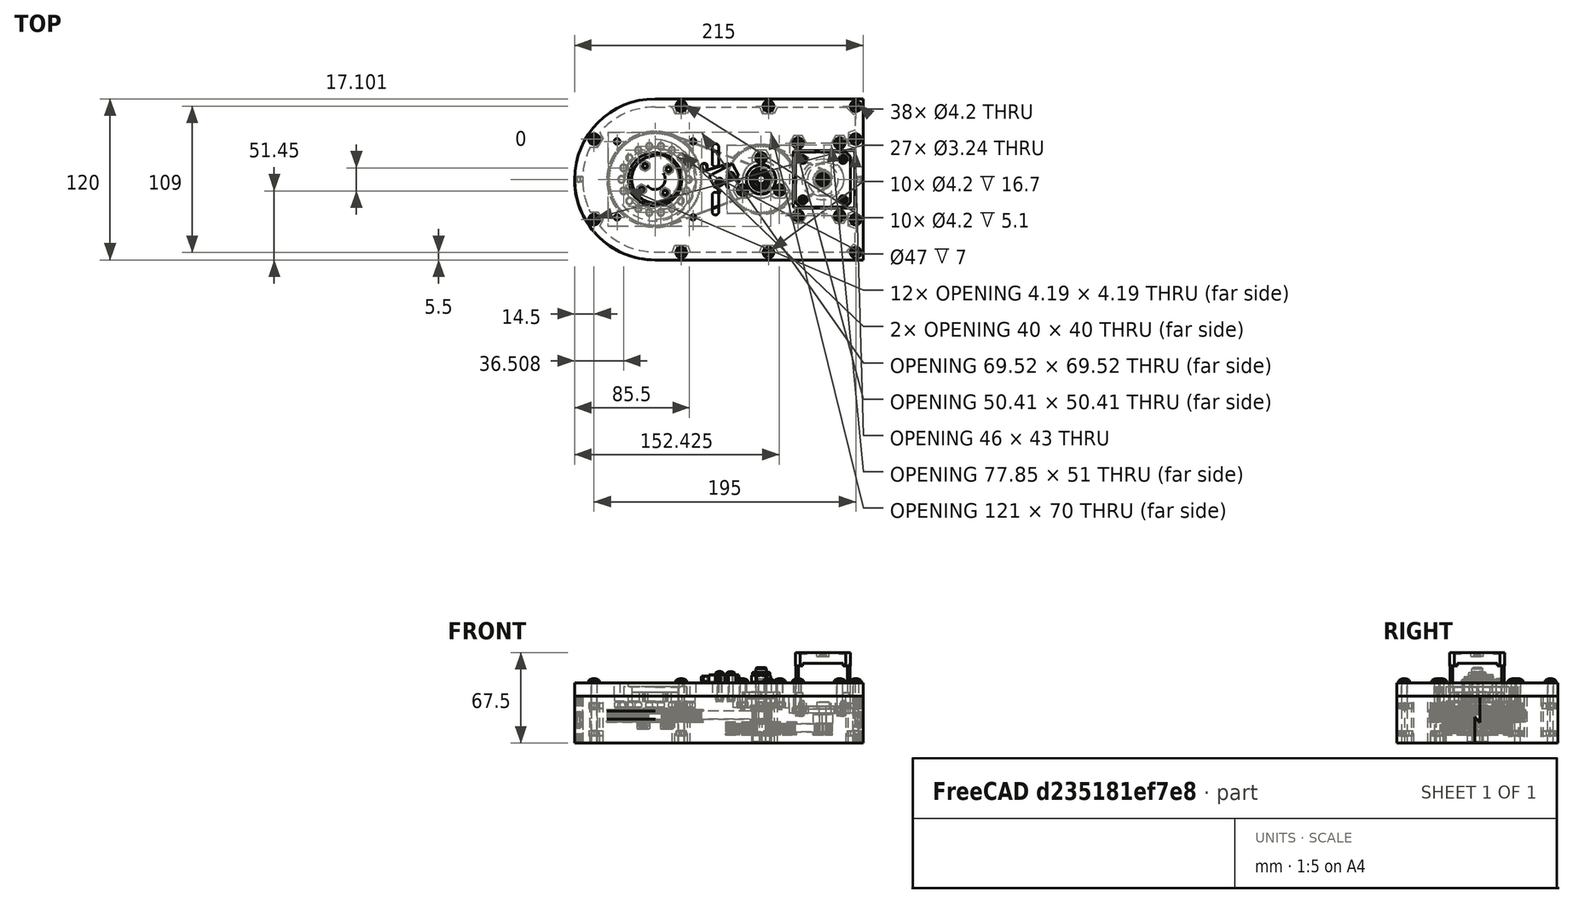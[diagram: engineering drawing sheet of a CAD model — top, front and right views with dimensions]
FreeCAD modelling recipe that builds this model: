
FCSTD DOCUMENT  (FreeCAD 0.19R24276 (Git))
Label: Base_a2p
License: All rights reserved
LicenseURL: http://en.wikipedia.org/wiki/All_rights_reserved
objects: Part::FeaturePython×75, App::FeaturePython×48, Spreadsheet::Sheet×2
note: 75 computed .brp shape members not serialized (recipe doc carries the construction recipe); baked Part::Feature solids carry a one-line shape summary decoded from their .brp

FEATURE [Part::FeaturePython] b_Base_half_wall_001_  label="Base_half-wall_001"  # a2plus imported part (geometry in sourceFile) (typed FeaturePython)
  a2p_Version = V0.1
  fixedPosition = true
  objectType = a2pPart
  sourceFile = ./Base_half-wall.FCStd
  subassemblyImport = false
  timeLastImport = 1.62051e+09
  updateColors = true
FEATURE [Part::FeaturePython] b_Base_half_wall_001_001  label="Base_half-wall_002"  # a2plus imported part (geometry in sourceFile) (typed FeaturePython)
  Placement = pos=(1e-15,-2.9e-14,-1.35227e-08) rot=(1,0,0;3.14159rad)
  a2p_Version = V0.1
  fixedPosition = false
  objectType = a2pPart
  sourceFile = ./Base_half-wall.FCStd
  subassemblyImport = false
  timeLastImport = 1.62051e+09
  updateColors = true
FEATURE [App::FeaturePython] circularEdge_001  label="circularEdge_001__Base_half-wall_002"  # a2plus constraint (typed FeaturePython)
  Object1 = b_Base_half_wall_001_
  Object2 = b_Base_half_wall_001_001
  ParentTreeObject = -> b_Base_half_wall_001_
  SubElement1 = Edge96
  SubElement2 = Edge52
  Suppressed = false
  Type = circularEdge
  directionConstraint = 1
  lockRotation = true
  offset = 0
FEATURE [App::FeaturePython] circularEdge_001_mirror  label="circularEdge_001__Base_half-wall_001"  # a2plus constraint (typed FeaturePython)
  Object1 = b_Base_half_wall_001_
  Object2 = b_Base_half_wall_001_001
  ParentTreeObject = -> b_Base_half_wall_001_001
  SubElement1 = Edge96
  SubElement2 = Edge52
  Suppressed = false
  Type = circularEdge
  directionConstraint = 1
  lockRotation = true
  offset = 0
FEATURE [Part::FeaturePython] b_Base_plate_001_  label="Base_plate_001"  # a2plus imported part (geometry in sourceFile) (typed FeaturePython)
  Placement = pos=(5.66811e-10,1.89089e-08,27.5) rot=(1,0,0;3.14159rad)
  a2p_Version = V0.1
  fixedPosition = false
  objectType = a2pPart
  sourceFile = ./Base_plate.FCStd
  subassemblyImport = false
  timeLastImport = 1.62051e+09
  updateColors = true
FEATURE [App::FeaturePython] circularEdge_002  label="circularEdge_002__Base_half-wall_001"  # a2plus constraint (typed FeaturePython)
  Object1 = b_Base_plate_001_
  Object2 = b_Base_half_wall_001_
  ParentTreeObject = -> b_Base_plate_001_
  SubElement1 = Edge4
  SubElement2 = Edge100
  Suppressed = false
  Type = circularEdge
  directionConstraint = 1
  lockRotation = true
  offset = 0
FEATURE [App::FeaturePython] circularEdge_002_mirror  label="circularEdge_002__Base_plate_001"  # a2plus constraint (typed FeaturePython)
  Object1 = b_Base_plate_001_
  Object2 = b_Base_half_wall_001_
  ParentTreeObject = -> b_Base_half_wall_001_
  SubElement1 = Edge4
  SubElement2 = Edge100
  Suppressed = false
  Type = circularEdge
  directionConstraint = 1
  lockRotation = true
  offset = 0
FEATURE [Part::FeaturePython] b_Stepper_NEMA_17____20mm_shaft1_001_  label="Stepper NEMA 17 -  20mm shaft1_001"  # a2plus imported part (geometry in sourceFile) (typed FeaturePython)
  Placement = pos=(162.191,8.47956,71.0261) rot=(-0.708681,0.705529,0;3.14159rad)
  a2p_Version = V0.1
  fixedPosition = false
  objectType = a2pPart
  sourceFile = ./Stepper NEMA 17 -  20mm shaft.step
  subassemblyImport = false
  timeLastImport = 1.62049e+09
  updateColors = true
FEATURE [Part::FeaturePython] b_Base_motor_bracket_001_  label="Base_motor_bracket_001"  # a2plus imported part (geometry in sourceFile) (typed FeaturePython)
  Placement = pos=(122,-3.40918e-07,5) rot=(0,0,1;1.5708rad)
  a2p_Version = V0.1
  fixedPosition = false
  objectType = a2pPart
  sourceFile = ./Base_motor_bracket.FCStd
  subassemblyImport = false
  timeLastImport = 1.62051e+09
  updateColors = true
FEATURE [App::FeaturePython] circularEdge_003  label="circularEdge_003__Base_plate_001"  # a2plus constraint (typed FeaturePython)
  Object1 = b_Base_motor_bracket_001_
  Object2 = b_Base_plate_001_
  ParentTreeObject = -> b_Base_motor_bracket_001_
  SubElement1 = Edge30
  SubElement2 = Edge77
  Suppressed = false
  Type = circularEdge
  directionConstraint = 1
  lockRotation = false
  offset = 0
FEATURE [App::FeaturePython] circularEdge_003_mirror  label="circularEdge_003__Base_motor_bracket_001"  # a2plus constraint (typed FeaturePython)
  Object1 = b_Base_motor_bracket_001_
  Object2 = b_Base_plate_001_
  ParentTreeObject = -> b_Base_plate_001_
  SubElement1 = Edge30
  SubElement2 = Edge77
  Suppressed = false
  Type = circularEdge
  directionConstraint = 1
  lockRotation = false
  offset = 0
FEATURE [App::FeaturePython] axisCoincident_001  label="axisCoincident_001__Base_plate_001"  # a2plus constraint (typed FeaturePython)
  Object1 = b_Base_motor_bracket_001_
  Object2 = b_Base_plate_001_
  ParentTreeObject = -> b_Base_motor_bracket_001_
  SubElement1 = Face29
  SubElement2 = Face40
  Suppressed = false
  Type = axial
  directionConstraint = 1
  lockRotation = false
FEATURE [App::FeaturePython] axisCoincident_001_mirror  label="axisCoincident_001__Base_motor_bracket_001"  # a2plus constraint (typed FeaturePython)
  Object1 = b_Base_motor_bracket_001_
  Object2 = b_Base_plate_001_
  ParentTreeObject = -> b_Base_plate_001_
  SubElement1 = Face29
  SubElement2 = Face40
  Suppressed = false
  Type = axial
  directionConstraint = 1
  lockRotation = false
FEATURE [App::FeaturePython] planeCoincident_001  label="planeCoincident_001__Base_motor_bracket_001"  # a2plus constraint (typed FeaturePython)
  Object1 = b_Stepper_NEMA_17____20mm_shaft1_001_
  Object2 = b_Base_motor_bracket_001_
  ParentTreeObject = -> b_Stepper_NEMA_17____20mm_shaft1_001_
  SubElement1 = Face140
  SubElement2 = Face31
  Suppressed = false
  Type = plane
  directionConstraint = 1
  offset = 0
FEATURE [App::FeaturePython] planeCoincident_001_mirror  label="planeCoincident_001__Stepper NEMA 17 -  20mm shaft1_001"  # a2plus constraint (typed FeaturePython)
  Object1 = b_Stepper_NEMA_17____20mm_shaft1_001_
  Object2 = b_Base_motor_bracket_001_
  ParentTreeObject = -> b_Base_motor_bracket_001_
  SubElement1 = Face140
  SubElement2 = Face31
  Suppressed = false
  Type = plane
  directionConstraint = 1
  offset = 0
FEATURE [Part::FeaturePython] b_Base_dual_bearing_608_holder_001_  label="Base_dual_bearing_608_holder_001"  # a2plus imported part (geometry in sourceFile) (typed FeaturePython)
  Placement = pos=(79,3.47e-08,9) rot=(0,0,-1;1.5708rad)
  a2p_Version = V0.1
  fixedPosition = false
  objectType = a2pPart
  sourceFile = ./Base_dual_bearing_608_holder.FCStd
  subassemblyImport = false
  timeLastImport = 1.62052e+09
  updateColors = true
FEATURE [Part::FeaturePython] b_Ball_bearing_6081_001_  label="Ball_bearing_6081_001"  # a2plus imported part (geometry in sourceFile) (typed FeaturePython)
  Placement = pos=(79,4.49238e-08,9) rot=(0.999356,0.025383,0.025383;1.57144rad)
  a2p_Version = V0.1
  fixedPosition = false
  objectType = a2pPart
  sourceFile = ./Ball_bearing_608.step
  subassemblyImport = false
  timeLastImport = 1.62049e+09
  updateColors = true
FEATURE [App::FeaturePython] circularEdge_004  label="circularEdge_004__Base_plate_001"  # a2plus constraint (typed FeaturePython)
  Object1 = b_Base_dual_bearing_608_holder_001_
  Object2 = b_Base_plate_001_
  ParentTreeObject = -> b_Base_dual_bearing_608_holder_001_
  SubElement1 = Edge15
  SubElement2 = Edge158
  Suppressed = false
  Type = circularEdge
  directionConstraint = 1
  lockRotation = false
  offset = 0
FEATURE [App::FeaturePython] circularEdge_004_mirror  label="circularEdge_004__Base_dual_bearing_608_holder_001"  # a2plus constraint (typed FeaturePython)
  Object1 = b_Base_dual_bearing_608_holder_001_
  Object2 = b_Base_plate_001_
  ParentTreeObject = -> b_Base_plate_001_
  SubElement1 = Edge15
  SubElement2 = Edge158
  Suppressed = false
  Type = circularEdge
  directionConstraint = 1
  lockRotation = false
  offset = 0
FEATURE [App::FeaturePython] axisCoincident_004  label="axisCoincident_004__Base_plate_001"  # a2plus constraint (typed FeaturePython)
  Object1 = b_Base_dual_bearing_608_holder_001_
  Object2 = b_Base_plate_001_
  ParentTreeObject = -> b_Base_dual_bearing_608_holder_001_
  SubElement1 = Face33
  SubElement2 = Face44
  Suppressed = false
  Type = axial
  directionConstraint = 1
  lockRotation = false
FEATURE [App::FeaturePython] axisCoincident_004_mirror  label="axisCoincident_004__Base_dual_bearing_608_holder_001"  # a2plus constraint (typed FeaturePython)
  Object1 = b_Base_dual_bearing_608_holder_001_
  Object2 = b_Base_plate_001_
  ParentTreeObject = -> b_Base_plate_001_
  SubElement1 = Face33
  SubElement2 = Face44
  Suppressed = false
  Type = axial
  directionConstraint = 1
  lockRotation = false
FEATURE [App::FeaturePython] axisCoincident_005  label="axisCoincident_005__Base_dual_bearing_608_holder_001"  # a2plus constraint (typed FeaturePython)
  Object1 = b_Ball_bearing_6081_001_
  Object2 = b_Base_dual_bearing_608_holder_001_
  ParentTreeObject = -> b_Ball_bearing_6081_001_
  SubElement1 = Face15
  SubElement2 = Face25
  Suppressed = false
  Type = axial
  directionConstraint = 0
  lockRotation = false
FEATURE [App::FeaturePython] axisCoincident_005_mirror  label="axisCoincident_005__Ball_bearing_6081_001"  # a2plus constraint (typed FeaturePython)
  Object1 = b_Ball_bearing_6081_001_
  Object2 = b_Base_dual_bearing_608_holder_001_
  ParentTreeObject = -> b_Base_dual_bearing_608_holder_001_
  SubElement1 = Face15
  SubElement2 = Face25
  Suppressed = false
  Type = axial
  directionConstraint = 0
  lockRotation = false
FEATURE [App::FeaturePython] planeCoincident_002  label="planeCoincident_002__Base_dual_bearing_608_holder_001"  # a2plus constraint (typed FeaturePython)
  Object1 = b_Ball_bearing_6081_001_
  Object2 = b_Base_dual_bearing_608_holder_001_
  ParentTreeObject = -> b_Ball_bearing_6081_001_
  SubElement1 = Face13
  SubElement2 = Face51
  Suppressed = false
  Type = plane
  directionConstraint = 1
  offset = 0
FEATURE [App::FeaturePython] planeCoincident_002_mirror  label="planeCoincident_002__Ball_bearing_6081_001"  # a2plus constraint (typed FeaturePython)
  Object1 = b_Ball_bearing_6081_001_
  Object2 = b_Base_dual_bearing_608_holder_001_
  ParentTreeObject = -> b_Base_dual_bearing_608_holder_001_
  SubElement1 = Face13
  SubElement2 = Face51
  Suppressed = false
  Type = plane
  directionConstraint = 1
  offset = 0
FEATURE [Part::FeaturePython] b_Ball_bearing_6081_001_001  label="Ball_bearing_6081_002"  # a2plus imported part (geometry in sourceFile) (typed FeaturePython)
  Placement = pos=(79,2.39606e-08,20.5) rot=(1,0,0;1.5708rad)
  a2p_Version = V0.1
  fixedPosition = false
  objectType = a2pPart
  sourceFile = ./Ball_bearing_608.step
  subassemblyImport = false
  timeLastImport = 1.62049e+09
  updateColors = true
FEATURE [App::FeaturePython] planeCoincident_003  label="planeCoincident_003__Base_dual_bearing_608_holder_001"  # a2plus constraint (typed FeaturePython)
  Object1 = b_Ball_bearing_6081_001_001
  Object2 = b_Base_dual_bearing_608_holder_001_
  ParentTreeObject = -> b_Ball_bearing_6081_001_001
  SubElement1 = Face14
  SubElement2 = Face12
  Suppressed = false
  Type = plane
  directionConstraint = 0
  offset = 0
FEATURE [App::FeaturePython] planeCoincident_003_mirror  label="planeCoincident_003__Ball_bearing_6081_002"  # a2plus constraint (typed FeaturePython)
  Object1 = b_Ball_bearing_6081_001_001
  Object2 = b_Base_dual_bearing_608_holder_001_
  ParentTreeObject = -> b_Base_dual_bearing_608_holder_001_
  SubElement1 = Face14
  SubElement2 = Face12
  Suppressed = false
  Type = plane
  directionConstraint = 0
  offset = 0
FEATURE [App::FeaturePython] axisCoincident_006  label="axisCoincident_006__Base_plate_001"  # a2plus constraint (typed FeaturePython)
  Object1 = b_Ball_bearing_6081_001_001
  Object2 = b_Base_plate_001_
  ParentTreeObject = -> b_Ball_bearing_6081_001_001
  SubElement1 = Face15
  SubElement2 = Face16
  Suppressed = false
  Type = axial
  directionConstraint = 1
  lockRotation = false
FEATURE [App::FeaturePython] axisCoincident_006_mirror  label="axisCoincident_006__Ball_bearing_6081_002"  # a2plus constraint (typed FeaturePython)
  Object1 = b_Ball_bearing_6081_001_001
  Object2 = b_Base_plate_001_
  ParentTreeObject = -> b_Base_plate_001_
  SubElement1 = Face15
  SubElement2 = Face16
  Suppressed = false
  Type = axial
  directionConstraint = 1
  lockRotation = false
FEATURE [Part::FeaturePython] Washer  label="M8-Washer"  # Fasteners workbench fastener (typed FeaturePython)
  Placement = pos=(79,-9.53483e-09,10.5) rot=(0.382525,-0.923945,0;3.14159rad)
  baseObject = -> b_Ball_bearing_6081_001_ [Edge2]
  diameter = 8
  invert = true
  matchOuter = false
  offset = 0
  type = 3
FEATURE [Part::FeaturePython] b_Pulley_GT2_22t_80t1_001_  label="Pulley_GT2-22t_80t1_001"  # a2plus imported part (geometry in sourceFile) (typed FeaturePython)
  Placement = pos=(113.339,12.3739,16.25) rot=(0.970817,0.16958,0.16958;1.60041rad)
  a2p_Version = V0.1
  fixedPosition = false
  objectType = a2pPart
  sourceFile = ./Pulley_GT2-22t_80t.step
  subassemblyImport = false
  timeLastImport = 1.61956e+09
  updateColors = true
FEATURE [App::FeaturePython] circularEdge_005  label="circularEdge_005__Ball_bearing_6081_001"  # a2plus constraint (typed FeaturePython)
  Object1 = b_Pulley_GT2_22t_80t1_001_
  Object2 = b_Ball_bearing_6081_001_
  ParentTreeObject = -> b_Pulley_GT2_22t_80t1_001_
  SubElement1 = Edge2774
  SubElement2 = Edge9
  Suppressed = false
  Type = circularEdge
  directionConstraint = 1
  lockRotation = false
  offset = -1.45
FEATURE [App::FeaturePython] circularEdge_005_mirror  label="circularEdge_005__Pulley_GT2-22t_80t1_001"  # a2plus constraint (typed FeaturePython)
  Object1 = b_Pulley_GT2_22t_80t1_001_
  Object2 = b_Ball_bearing_6081_001_
  ParentTreeObject = -> b_Ball_bearing_6081_001_
  SubElement1 = Edge2774
  SubElement2 = Edge9
  Suppressed = false
  Type = circularEdge
  directionConstraint = 1
  lockRotation = false
  offset = -1.45
FEATURE [Part::FeaturePython] Screw  label="M8x50-Screw"  # Fasteners workbench fastener (typed FeaturePython)
  Placement = pos=(79,-2.84139e-07,-11.25) rot=(0.225502,-0.974243,0;3.14159rad)
  baseObject = -> b_Pulley_GT2_22t_80t1_001_ [Edge2261]
  diameter = 9
  invert = false
  length = 7
  lengthCustom = 50
  matchOuter = false
  offset = 0
  thread = false
  type = 28
FEATURE [Part::FeaturePython] Nut  label="M8-Nut"  # Fasteners workbench fastener (typed FeaturePython)
  Placement = pos=(79,1.24719e-08,27.5) rot=(0,0,1;0rad)
  baseObject = -> b_Ball_bearing_6081_001_001 [Edge39]
  diameter = 6
  invert = true
  matchOuter = false
  offset = 0
  thread = false
  type = 5
FEATURE [Part::FeaturePython] b_Pulley_GT2_20t1_001_  label="Pulley_GT2-20t1_001"  # a2plus imported part (geometry in sourceFile) (typed FeaturePython)
  Placement = pos=(200.139,-14.0632,16.25) rot=(-0.984181,-0.125275,-0.125275;4.69644rad)
  a2p_Version = V0.1
  fixedPosition = false
  objectType = a2pPart
  sourceFile = ./Pulley_GT2-20t.step
  subassemblyImport = false
  timeLastImport = 1.61956e+09
  updateColors = true
FEATURE [App::FeaturePython] axisCoincident_007  label="axisCoincident_007__Stepper NEMA 17 -  20mm shaft1_001"  # a2plus constraint (typed FeaturePython)
  Object1 = b_Pulley_GT2_20t1_001_
  Object2 = b_Stepper_NEMA_17____20mm_shaft1_001_
  ParentTreeObject = -> b_Pulley_GT2_20t1_001_
  SubElement1 = Face190
  SubElement2 = Face21
  Suppressed = false
  Type = axial
  directionConstraint = 1
  lockRotation = false
FEATURE [App::FeaturePython] axisCoincident_007_mirror  label="axisCoincident_007__Pulley_GT2-20t1_001"  # a2plus constraint (typed FeaturePython)
  Object1 = b_Pulley_GT2_20t1_001_
  Object2 = b_Stepper_NEMA_17____20mm_shaft1_001_
  ParentTreeObject = -> b_Stepper_NEMA_17____20mm_shaft1_001_
  SubElement1 = Face190
  SubElement2 = Face21
  Suppressed = false
  Type = axial
  directionConstraint = 1
  lockRotation = false
FEATURE [App::FeaturePython] planeCoincident_004  label="planeCoincident_004__Pulley_GT2-22t_80t1_001"  # a2plus constraint (typed FeaturePython)
  Object1 = b_Pulley_GT2_20t1_001_
  Object2 = b_Pulley_GT2_22t_80t1_001_
  ParentTreeObject = -> b_Pulley_GT2_20t1_001_
  SubElement1 = Face188
  SubElement2 = Face744
  Suppressed = false
  Type = plane
  directionConstraint = 0
  offset = 0
FEATURE [App::FeaturePython] planeCoincident_004_mirror  label="planeCoincident_004__Pulley_GT2-20t1_001"  # a2plus constraint (typed FeaturePython)
  Object1 = b_Pulley_GT2_20t1_001_
  Object2 = b_Pulley_GT2_22t_80t1_001_
  ParentTreeObject = -> b_Pulley_GT2_22t_80t1_001_
  SubElement1 = Face188
  SubElement2 = Face744
  Suppressed = false
  Type = plane
  directionConstraint = 0
  offset = 0
FEATURE [Part::FeaturePython] b_Ball_bearing_68071_001_  label="Ball_bearing_68071_001"  # a2plus imported part (geometry in sourceFile) (typed FeaturePython)
  Placement = pos=(5.66811e-10,-1.00196e-07,17.5) rot=(1,0,0;1.5708rad)
  a2p_Version = V0.1
  fixedPosition = false
  objectType = a2pPart
  sourceFile = ./Ball_bearing_6807.step
  subassemblyImport = false
  timeLastImport = 1.62051e+09
  updateColors = true
FEATURE [App::FeaturePython] circularEdge_006  label="circularEdge_006__Base_plate_001"  # a2plus constraint (typed FeaturePython)
  Object1 = b_Ball_bearing_68071_001_
  Object2 = b_Base_plate_001_
  ParentTreeObject = -> b_Ball_bearing_68071_001_
  SubElement1 = Edge41
  SubElement2 = Edge154
  Suppressed = false
  Type = circularEdge
  directionConstraint = 1
  lockRotation = false
  offset = 0
FEATURE [App::FeaturePython] circularEdge_006_mirror  label="circularEdge_006__Ball_bearing_68071_001"  # a2plus constraint (typed FeaturePython)
  Object1 = b_Ball_bearing_68071_001_
  Object2 = b_Base_plate_001_
  ParentTreeObject = -> b_Base_plate_001_
  SubElement1 = Edge41
  SubElement2 = Edge154
  Suppressed = false
  Type = circularEdge
  directionConstraint = 1
  lockRotation = false
  offset = 0
FEATURE [Part::FeaturePython] b_Thrust_bearing_511081_001_  label="Thrust_bearing_511081_001"  # a2plus imported part (geometry in sourceFile) (typed FeaturePython)
  Placement = pos=(5.66811e-10,1.89089e-08,17.5) rot=(-1,0,0;1.5708rad)
  a2p_Version = V0.1
  fixedPosition = false
  objectType = a2pPart
  sourceFile = ./Thrust_bearing_51108.step
  subassemblyImport = false
  timeLastImport = 1.62049e+09
  updateColors = true
FEATURE [App::FeaturePython] circularEdge_007  label="circularEdge_007__Thrust_bearing_511081_001"  # a2plus constraint (typed FeaturePython)
  Object1 = b_Base_plate_001_
  Object2 = b_Thrust_bearing_511081_001_
  ParentTreeObject = -> b_Base_plate_001_
  SubElement1 = Edge57
  SubElement2 = Edge1
  Suppressed = false
  Type = circularEdge
  directionConstraint = 1
  lockRotation = false
  offset = 0
FEATURE [App::FeaturePython] circularEdge_007_mirror  label="circularEdge_007__Base_plate_001"  # a2plus constraint (typed FeaturePython)
  Object1 = b_Base_plate_001_
  Object2 = b_Thrust_bearing_511081_001_
  ParentTreeObject = -> b_Thrust_bearing_511081_001_
  SubElement1 = Edge57
  SubElement2 = Edge1
  Suppressed = false
  Type = circularEdge
  directionConstraint = 1
  lockRotation = false
  offset = 0
FEATURE [Part::FeaturePython] b_Pulley_GT2_110t1_001_  label="Pulley_GT2-110t1_001"  # a2plus imported part (geometry in sourceFile) (typed FeaturePython)
  Placement = pos=(-25.496,34.003,17.5) rot=(0.816457,-0.408288,-0.408288;1.7722rad)
  a2p_Version = V0.1
  fixedPosition = false
  objectType = a2pPart
  sourceFile = ./Pulley_GT2-110t.step
  subassemblyImport = false
  timeLastImport = 1.61956e+09
  updateColors = true
FEATURE [App::FeaturePython] circularEdge_008  label="circularEdge_008__Thrust_bearing_511081_001"  # a2plus constraint (typed FeaturePython)
  Object1 = b_Pulley_GT2_110t1_001_
  Object2 = b_Thrust_bearing_511081_001_
  ParentTreeObject = -> b_Pulley_GT2_110t1_001_
  SubElement1 = Edge3003
  SubElement2 = Edge32
  Suppressed = false
  Type = circularEdge
  directionConstraint = 0
  lockRotation = false
  offset = 0
FEATURE [App::FeaturePython] circularEdge_008_mirror  label="circularEdge_008__Pulley_GT2-110t1_001"  # a2plus constraint (typed FeaturePython)
  Object1 = b_Pulley_GT2_110t1_001_
  Object2 = b_Thrust_bearing_511081_001_
  ParentTreeObject = -> b_Thrust_bearing_511081_001_
  SubElement1 = Edge3003
  SubElement2 = Edge32
  Suppressed = false
  Type = circularEdge
  directionConstraint = 0
  lockRotation = false
  offset = 0
FEATURE [Part::FeaturePython] b_Belt_GT2_200mm_20_801_001_  label="Belt_GT2_200mm_20-801_001"  # a2plus imported part (geometry in sourceFile) (typed FeaturePython)
  Placement = pos=(79,1.2245e-07,-3.05) rot=(-0.001135,-0.707106,0.707106;3.13932rad)
  a2p_Version = V0.1
  fixedPosition = false
  objectType = a2pPart
  sourceFile = ./Belt_GT2_200mm_20-80.step
  subassemblyImport = false
  timeLastImport = 1.62051e+09
  updateColors = true
FEATURE [App::FeaturePython] circularEdge_009  label="circularEdge_009__Pulley_GT2-20t1_001"  # a2plus constraint (typed FeaturePython)
  Object1 = b_Belt_GT2_200mm_20_801_001_
  Object2 = b_Pulley_GT2_20t1_001_
  ParentTreeObject = -> b_Belt_GT2_200mm_20_801_001_
  SubElement1 = Edge27
  SubElement2 = Edge559
  Suppressed = false
  Type = circularEdge
  directionConstraint = 0
  lockRotation = false
  offset = 0
FEATURE [App::FeaturePython] circularEdge_009_mirror  label="circularEdge_009__Belt_GT2_200mm_20-801_001"  # a2plus constraint (typed FeaturePython)
  Object1 = b_Belt_GT2_200mm_20_801_001_
  Object2 = b_Pulley_GT2_20t1_001_
  ParentTreeObject = -> b_Pulley_GT2_20t1_001_
  SubElement1 = Edge27
  SubElement2 = Edge559
  Suppressed = false
  Type = circularEdge
  directionConstraint = 0
  lockRotation = false
  offset = 0
FEATURE [App::FeaturePython] axisCoincident_002  label="axisCoincident_002__Pulley_GT2-22t_80t1_001"  # a2plus constraint (typed FeaturePython)
  Object1 = b_Belt_GT2_200mm_20_801_001_
  Object2 = b_Pulley_GT2_22t_80t1_001_
  ParentTreeObject = -> b_Belt_GT2_200mm_20_801_001_
  SubElement1 = Face2
  SubElement2 = Face29
  Suppressed = false
  Type = axial
  directionConstraint = 0
  lockRotation = false
FEATURE [App::FeaturePython] axisCoincident_002_mirror  label="axisCoincident_002__Belt_GT2_200mm_20-801_001"  # a2plus constraint (typed FeaturePython)
  Object1 = b_Belt_GT2_200mm_20_801_001_
  Object2 = b_Pulley_GT2_22t_80t1_001_
  ParentTreeObject = -> b_Pulley_GT2_22t_80t1_001_
  SubElement1 = Face2
  SubElement2 = Face29
  Suppressed = false
  Type = axial
  directionConstraint = 0
  lockRotation = false
FEATURE [App::FeaturePython] axisPlaneParallel_001  label="axisPlaneParallel_001__Base_motor_bracket_001"  # a2plus constraint (typed FeaturePython)
  Object1 = b_Stepper_NEMA_17____20mm_shaft1_001_
  Object2 = b_Base_motor_bracket_001_
  ParentTreeObject = -> b_Stepper_NEMA_17____20mm_shaft1_001_
  SubElement1 = Face11
  SubElement2 = Face38
  Suppressed = false
  Type = axisPlaneParallel
FEATURE [App::FeaturePython] axisPlaneParallel_001_mirror  label="axisPlaneParallel_001__Stepper NEMA 17 -  20mm shaft1_001"  # a2plus constraint (typed FeaturePython)
  Object1 = b_Stepper_NEMA_17____20mm_shaft1_001_
  Object2 = b_Base_motor_bracket_001_
  ParentTreeObject = -> b_Base_motor_bracket_001_
  SubElement1 = Face11
  SubElement2 = Face38
  Suppressed = false
  Type = axisPlaneParallel
FEATURE [App::FeaturePython] axisPlaneParallel_002  label="axisPlaneParallel_002__Base_motor_bracket_001"  # a2plus constraint (typed FeaturePython)
  Object1 = b_Stepper_NEMA_17____20mm_shaft1_001_
  Object2 = b_Base_motor_bracket_001_
  ParentTreeObject = -> b_Stepper_NEMA_17____20mm_shaft1_001_
  SubElement1 = Face8
  SubElement2 = Face42
  Suppressed = false
  Type = axisPlaneParallel
FEATURE [App::FeaturePython] axisPlaneParallel_002_mirror  label="axisPlaneParallel_002__Stepper NEMA 17 -  20mm shaft1_001"  # a2plus constraint (typed FeaturePython)
  Object1 = b_Stepper_NEMA_17____20mm_shaft1_001_
  Object2 = b_Base_motor_bracket_001_
  ParentTreeObject = -> b_Base_motor_bracket_001_
  SubElement1 = Face8
  SubElement2 = Face42
  Suppressed = false
  Type = axisPlaneParallel
FEATURE [Part::FeaturePython] b_Belt_GT2_200mm_22_1101_001_  label="Belt_GT2_200mm_22-1101_001"  # a2plus imported part (geometry in sourceFile) (typed FeaturePython)
  Placement = pos=(-8.54781e-07,1.57583e-05,0.350008) rot=(0,0.707107,0.707107;3.14159rad)
  a2p_Version = V0.1
  fixedPosition = false
  objectType = a2pPart
  sourceFile = ./Belt_GT2_200mm_22-110.step
  subassemblyImport = false
  timeLastImport = 1.62051e+09
  updateColors = true
FEATURE [App::FeaturePython] circularEdge_010  label="circularEdge_010__Pulley_GT2-22t_80t1_001"  # a2plus constraint (typed FeaturePython)
  Object1 = b_Belt_GT2_200mm_22_1101_001_
  Object2 = b_Pulley_GT2_22t_80t1_001_
  ParentTreeObject = -> b_Belt_GT2_200mm_22_1101_001_
  SubElement1 = Edge20
  SubElement2 = Edge5
  Suppressed = false
  Type = circularEdge
  directionConstraint = 1
  lockRotation = false
  offset = 0
FEATURE [App::FeaturePython] circularEdge_010_mirror  label="circularEdge_010__Belt_GT2_200mm_22-1101_001"  # a2plus constraint (typed FeaturePython)
  Object1 = b_Belt_GT2_200mm_22_1101_001_
  Object2 = b_Pulley_GT2_22t_80t1_001_
  ParentTreeObject = -> b_Pulley_GT2_22t_80t1_001_
  SubElement1 = Edge20
  SubElement2 = Edge5
  Suppressed = false
  Type = circularEdge
  directionConstraint = 1
  lockRotation = false
  offset = 0
FEATURE [Part::FeaturePython] b_Switch_endstop1_001_  label="Switch_endstop1_001"  # a2plus imported part (geometry in sourceFile) (typed FeaturePython)
  Placement = pos=(51.2426,2.55496,33.5002) rot=(0.241879,-0.970307,4e-06;3.14155rad)
  a2p_Version = V0.1
  fixedPosition = false
  objectType = a2pPart
  sourceFile = ./Switch_endstop.step
  subassemblyImport = false
  timeLastImport = 1598970250
  updateColors = true
FEATURE [App::FeaturePython] circularEdge_011  label="circularEdge_011__Base_plate_001"  # a2plus constraint (typed FeaturePython)
  Object1 = b_Switch_endstop1_001_
  Object2 = b_Base_plate_001_
  ParentTreeObject = -> b_Switch_endstop1_001_
  SubElement1 = Edge36
  SubElement2 = Edge52
  Suppressed = false
  Type = circularEdge
  directionConstraint = 0
  lockRotation = false
  offset = 0
FEATURE [App::FeaturePython] circularEdge_011_mirror  label="circularEdge_011__Switch_endstop1_001"  # a2plus constraint (typed FeaturePython)
  Object1 = b_Switch_endstop1_001_
  Object2 = b_Base_plate_001_
  ParentTreeObject = -> b_Base_plate_001_
  SubElement1 = Edge36
  SubElement2 = Edge52
  Suppressed = false
  Type = circularEdge
  directionConstraint = 0
  lockRotation = false
  offset = 0
FEATURE [App::FeaturePython] axisCoincident_003  label="axisCoincident_003__Switch_endstop1_001"  # a2plus constraint (typed FeaturePython)
  Object1 = b_Base_plate_001_
  Object2 = b_Switch_endstop1_001_
  ParentTreeObject = -> b_Base_plate_001_
  SubElement1 = Face46
  SubElement2 = Face10
  Suppressed = false
  Type = axial
  directionConstraint = 1
  lockRotation = false
FEATURE [App::FeaturePython] axisCoincident_003_mirror  label="axisCoincident_003__Base_plate_001"  # a2plus constraint (typed FeaturePython)
  Object1 = b_Base_plate_001_
  Object2 = b_Switch_endstop1_001_
  ParentTreeObject = -> b_Switch_endstop1_001_
  SubElement1 = Face46
  SubElement2 = Face10
  Suppressed = false
  Type = axial
  directionConstraint = 1
  lockRotation = false
FEATURE [Part::FeaturePython] Screw001  label="M4x20-Screw"  # Fasteners workbench fastener (typed FeaturePython)
  Placement = pos=(149.5,-30,27.5) rot=(0,0,1;0rad)
  baseObject = -> b_Base_plate_001_ [Edge44]
  diameter = 6
  invert = true
  length = 7
  lengthCustom = 20
  matchOuter = false
  offset = 0
  thread = false
  type = 34
FEATURE [Part::FeaturePython] Screw002  label="M4x20-Screw001"  # Fasteners workbench fastener (typed FeaturePython)
  Placement = pos=(149.5,-54.5,27.5) rot=(0,0,1;0rad)
  baseObject = -> b_Base_plate_001_ [Edge40]
  diameter = 6
  invert = true
  length = 7
  lengthCustom = 20
  matchOuter = false
  offset = 0
  thread = false
  type = 34
FEATURE [Part::FeaturePython] Screw003  label="M4x20-Screw002"  # Fasteners workbench fastener (typed FeaturePython)
  Placement = pos=(84.5,-54.5,27.5) rot=(0,0,1;0rad)
  baseObject = -> b_Base_plate_001_ [Edge41]
  diameter = 6
  invert = true
  length = 7
  lengthCustom = 20
  matchOuter = false
  offset = 0
  thread = false
  type = 34
FEATURE [Part::FeaturePython] Screw004  label="M4x20-Screw003"  # Fasteners workbench fastener (typed FeaturePython)
  Placement = pos=(19.5,-54.5,27.5) rot=(0,0,1;0rad)
  baseObject = -> b_Base_plate_001_ [Edge31]
  diameter = 6
  invert = true
  length = 7
  lengthCustom = 20
  matchOuter = false
  offset = 0
  thread = false
  type = 34
FEATURE [Part::FeaturePython] Screw005  label="M4x20-Screw004"  # Fasteners workbench fastener (typed FeaturePython)
  Placement = pos=(-45.5,-30,27.5) rot=(0,0,1;0rad)
  baseObject = -> b_Base_plate_001_ [Edge32]
  diameter = 6
  invert = true
  length = 7
  lengthCustom = 20
  matchOuter = false
  offset = 0
  thread = false
  type = 34
FEATURE [Part::FeaturePython] Screw006  label="M4x20-Screw005"  # Fasteners workbench fastener (typed FeaturePython)
  Placement = pos=(-45.5,30,27.5) rot=(0,0,1;0rad)
  baseObject = -> b_Base_plate_001_ [Edge33]
  diameter = 6
  invert = true
  length = 7
  lengthCustom = 20
  matchOuter = false
  offset = 0
  thread = false
  type = 34
FEATURE [Part::FeaturePython] Screw007  label="M4x20-Screw006"  # Fasteners workbench fastener (typed FeaturePython)
  Placement = pos=(19.5,54.5,27.5) rot=(0,0,1;0rad)
  baseObject = -> b_Base_plate_001_ [Edge30]
  diameter = 6
  invert = true
  length = 7
  lengthCustom = 20
  matchOuter = false
  offset = 0
  thread = false
  type = 34
FEATURE [Part::FeaturePython] Screw008  label="M4x20-Screw007"  # Fasteners workbench fastener (typed FeaturePython)
  Placement = pos=(84.5,54.5,27.5) rot=(0,0,1;0rad)
  baseObject = -> b_Base_plate_001_ [Edge48]
  diameter = 6
  invert = true
  length = 7
  lengthCustom = 20
  matchOuter = false
  offset = 0
  thread = false
  type = 34
FEATURE [Part::FeaturePython] Screw009  label="M4x20-Screw008"  # Fasteners workbench fastener (typed FeaturePython)
  Placement = pos=(149.5,54.5,27.5) rot=(0,0,1;0rad)
  baseObject = -> b_Base_plate_001_ [Edge39]
  diameter = 6
  invert = true
  length = 7
  lengthCustom = 20
  matchOuter = false
  offset = 0
  thread = false
  type = 34
FEATURE [Part::FeaturePython] Screw010  label="M4x20-Screw009"  # Fasteners workbench fastener (typed FeaturePython)
  Placement = pos=(149.5,30,27.5) rot=(0,0,1;0rad)
  baseObject = -> b_Base_plate_001_ [Edge46]
  diameter = 6
  invert = true
  length = 7
  lengthCustom = 20
  matchOuter = false
  offset = 0
  thread = false
  type = 34
FEATURE [Part::FeaturePython] Screw011  label="M4x25-Screw"  # Fasteners workbench fastener (typed FeaturePython)
  Placement = pos=(137.5,27,27.5) rot=(0,0,1;0rad)
  baseObject = -> b_Base_plate_001_ [Edge43]
  diameter = 6
  invert = true
  length = 8
  lengthCustom = 25
  matchOuter = false
  offset = 0
  thread = false
  type = 34
FEATURE [Part::FeaturePython] Screw012  label="M4x25-Screw001"  # Fasteners workbench fastener (typed FeaturePython)
  Placement = pos=(106.5,27,27.5) rot=(0,0,1;0rad)
  baseObject = -> b_Base_plate_001_ [Edge42]
  diameter = 6
  invert = true
  length = 8
  lengthCustom = 25
  matchOuter = false
  offset = 0
  thread = false
  type = 34
FEATURE [Part::FeaturePython] Screw013  label="M4x25-Screw002"  # Fasteners workbench fastener (typed FeaturePython)
  Placement = pos=(106.5,-27,27.5) rot=(0,0,1;0rad)
  baseObject = -> b_Base_plate_001_ [Edge45]
  diameter = 6
  invert = true
  length = 8
  lengthCustom = 25
  matchOuter = false
  offset = 0
  thread = false
  type = 34
FEATURE [Part::FeaturePython] Screw014  label="M4x25-Screw003"  # Fasteners workbench fastener (typed FeaturePython)
  Placement = pos=(137.5,-27,27.5) rot=(0,0,1;0rad)
  baseObject = -> b_Base_plate_001_ [Edge47]
  diameter = 6
  invert = true
  length = 8
  lengthCustom = 25
  matchOuter = false
  offset = 0
  thread = false
  type = 34
FEATURE [Part::FeaturePython] Screw015  label="M4x20-Screw014"  # Fasteners workbench fastener (typed FeaturePython)
  Placement = pos=(79,16,27.5) rot=(0,0,1;0rad)
  baseObject = -> b_Base_plate_001_ [Edge49]
  diameter = 6
  invert = true
  length = 7
  lengthCustom = 20
  matchOuter = false
  offset = 0
  thread = false
  type = 34
FEATURE [Part::FeaturePython] Screw016  label="M4x20-Screw015"  # Fasteners workbench fastener (typed FeaturePython)
  Placement = pos=(92.8564,-8,27.5) rot=(0,0,1;0rad)
  baseObject = -> b_Base_plate_001_ [Edge50]
  diameter = 6
  invert = true
  length = 7
  lengthCustom = 20
  matchOuter = false
  offset = 0
  thread = false
  type = 34
FEATURE [Part::FeaturePython] Screw017  label="M4x20-Screw016"  # Fasteners workbench fastener (typed FeaturePython)
  Placement = pos=(65.1436,-8,27.5) rot=(0,0,1;0rad)
  baseObject = -> b_Base_plate_001_ [Edge38]
  diameter = 6
  invert = true
  length = 7
  lengthCustom = 20
  matchOuter = false
  offset = 0
  thread = false
  type = 34
FEATURE [Part::FeaturePython] Nut001  label="M4-Nut"  # Fasteners workbench fastener (typed FeaturePython)
  Placement = pos=(19.5,54.5,-8.5) rot=(-1,0,0;3.14159rad)
  baseObject = -> b_Base_half_wall_001_ [Edge358]
  diameter = 6
  invert = true
  matchOuter = false
  offset = 0
  thread = false
  type = 7
FEATURE [Part::FeaturePython] Nut002  label="M4-Nut001"  # Fasteners workbench fastener (typed FeaturePython)
  Placement = pos=(84.5,54.5,-8.5) rot=(-1,0,0;3.14159rad)
  baseObject = -> b_Base_half_wall_001_ [Edge331]
  diameter = 6
  invert = true
  matchOuter = false
  offset = 0
  thread = false
  type = 7
FEATURE [Part::FeaturePython] Nut003  label="M4-Nut002"  # Fasteners workbench fastener (typed FeaturePython)
  Placement = pos=(84.5,54.5,12.1) rot=(-1,0,0;3.14159rad)
  baseObject = -> b_Base_half_wall_001_ [Edge317]
  diameter = 6
  invert = true
  matchOuter = false
  offset = 0
  thread = false
  type = 7
FEATURE [Part::FeaturePython] Nut004  label="M4-Nut003"  # Fasteners workbench fastener (typed FeaturePython)
  Placement = pos=(149.5,54.5,-8.5) rot=(-1,0,0;3.14159rad)
  baseObject = -> b_Base_half_wall_001_ [Edge270]
  diameter = 6
  invert = true
  matchOuter = false
  offset = 0
  thread = false
  type = 7
FEATURE [Part::FeaturePython] Nut005  label="M4-Nut004"  # Fasteners workbench fastener (typed FeaturePython)
  Placement = pos=(149.5,54.5,12.1) rot=(-1,0,0;3.14159rad)
  baseObject = -> b_Base_half_wall_001_ [Edge284]
  diameter = 6
  invert = true
  matchOuter = false
  offset = 0
  thread = false
  type = 7
FEATURE [Part::FeaturePython] Nut006  label="M4-Nut005"  # Fasteners workbench fastener (typed FeaturePython)
  Placement = pos=(149.5,30,-8.5) rot=(-1,0,0;3.14159rad)
  baseObject = -> b_Base_half_wall_001_ [Edge111]
  diameter = 6
  invert = true
  matchOuter = false
  offset = 0
  thread = false
  type = 7
FEATURE [Part::FeaturePython] Nut007  label="M4-Nut006"  # Fasteners workbench fastener (typed FeaturePython)
  Placement = pos=(149.5,30,12.1) rot=(-1,0,0;3.14159rad)
  baseObject = -> b_Base_half_wall_001_ [Edge7]
  diameter = 6
  invert = true
  matchOuter = false
  offset = 0
  thread = false
  type = 7
FEATURE [Part::FeaturePython] Nut008  label="M4-Nut007"  # Fasteners workbench fastener (typed FeaturePython)
  Placement = pos=(-45.5,30,12.1) rot=(-1,0,0;3.14159rad)
  baseObject = -> b_Base_half_wall_001_ [Edge311]
  diameter = 6
  invert = true
  matchOuter = false
  offset = 0
  thread = false
  type = 7
FEATURE [Part::FeaturePython] Nut009  label="M4-Nut008"  # Fasteners workbench fastener (typed FeaturePython)
  Placement = pos=(-45.5,30,-8.5) rot=(-1,0,0;3.14159rad)
  baseObject = -> b_Base_half_wall_001_ [Edge297]
  diameter = 6
  invert = true
  matchOuter = false
  offset = 0
  thread = false
  type = 7
FEATURE [Part::FeaturePython] Nut010  label="M4-Nut029"  # Fasteners workbench fastener (typed FeaturePython)
  Placement = pos=(149.5,-30,-8.5) rot=(1,0,0;3.14159rad)
  baseObject = -> b_Base_half_wall_001_001 [Edge28]
  diameter = 6
  invert = false
  matchOuter = false
  offset = 0
  thread = false
  type = 7
FEATURE [Part::FeaturePython] Nut011  label="M4-Nut028"  # Fasteners workbench fastener (typed FeaturePython)
  Placement = pos=(149.5,-30,12.1) rot=(1,0,0;3.14159rad)
  baseObject = -> b_Base_half_wall_001_001 [Edge118]
  diameter = 6
  invert = false
  matchOuter = false
  offset = 0
  thread = false
  type = 7
FEATURE [Part::FeaturePython] Nut012  label="M4-Nut027"  # Fasteners workbench fastener (typed FeaturePython)
  Placement = pos=(149.5,-54.5,-8.5) rot=(1,0,0;3.14159rad)
  baseObject = -> b_Base_half_wall_001_001 [Edge278]
  diameter = 6
  invert = false
  matchOuter = false
  offset = 0
  thread = false
  type = 7
FEATURE [Part::FeaturePython] Nut013  label="M4-Nut026"  # Fasteners workbench fastener (typed FeaturePython)
  Placement = pos=(149.5,-54.5,12.1) rot=(1,0,0;3.14159rad)
  baseObject = -> b_Base_half_wall_001_001 [Edge218]
  diameter = 6
  invert = false
  matchOuter = false
  offset = 0
  thread = false
  type = 7
FEATURE [Part::FeaturePython] Nut014  label="M4-Nut025"  # Fasteners workbench fastener (typed FeaturePython)
  Placement = pos=(84.5,-54.5,12.1) rot=(1,0,0;3.14159rad)
  baseObject = -> b_Base_half_wall_001_001 [Edge216]
  diameter = 6
  invert = false
  matchOuter = false
  offset = 0
  thread = false
  type = 7
FEATURE [Part::FeaturePython] Nut015  label="M4-Nut024"  # Fasteners workbench fastener (typed FeaturePython)
  Placement = pos=(84.5,-54.5,-8.5) rot=(1,0,0;3.14159rad)
  baseObject = -> b_Base_half_wall_001_001 [Edge324]
  diameter = 6
  invert = false
  matchOuter = false
  offset = 0
  thread = false
  type = 7
FEATURE [Part::FeaturePython] Nut016  label="M4-Nut023"  # Fasteners workbench fastener (typed FeaturePython)
  Placement = pos=(19.5,-54.5,12.1) rot=(1,0,0;3.14159rad)
  baseObject = -> b_Base_half_wall_001_001 [Edge214]
  diameter = 6
  invert = false
  matchOuter = false
  offset = 0
  thread = false
  type = 7
FEATURE [Part::FeaturePython] Nut017  label="M4-Nut022"  # Fasteners workbench fastener (typed FeaturePython)
  Placement = pos=(19.5,-54.5,-8.5) rot=(1,0,0;3.14159rad)
  baseObject = -> b_Base_half_wall_001_001 [Edge351]
  diameter = 6
  invert = false
  matchOuter = false
  offset = 0
  thread = false
  type = 7
FEATURE [Part::FeaturePython] Nut018  label="M4-Nut021"  # Fasteners workbench fastener (typed FeaturePython)
  Placement = pos=(-45.5,-30,12.1) rot=(1,0,0;3.14159rad)
  baseObject = -> b_Base_half_wall_001_001 [Edge211]
  diameter = 6
  invert = false
  matchOuter = false
  offset = 0
  thread = false
  type = 7
FEATURE [Part::FeaturePython] Nut019  label="M4-Nut020"  # Fasteners workbench fastener (typed FeaturePython)
  Placement = pos=(-45.5,-30,-8.5) rot=(1,0,0;3.14159rad)
  baseObject = -> b_Base_half_wall_001_001 [Edge305]
  diameter = 6
  invert = false
  matchOuter = false
  offset = 0
  thread = false
  type = 7
FEATURE [Part::FeaturePython] Nut020  label="M4-Nut019"  # Fasteners workbench fastener (typed FeaturePython)
  Placement = pos=(19.5,54.5,12.1) rot=(-1,0,0;3.14159rad)
  baseObject = -> b_Base_half_wall_001_ [Edge344]
  diameter = 6
  invert = true
  matchOuter = false
  offset = 0
  thread = false
  type = 7
FEATURE [Part::FeaturePython] Nut021  label="M4-Nut034"  # Fasteners workbench fastener (typed FeaturePython)
  Placement = pos=(137.5,-27,9) rot=(0.995904,0.090421,0;3.14159rad)
  baseObject = -> b_Base_motor_bracket_001_ [Edge83]
  diameter = 6
  invert = false
  matchOuter = false
  offset = 0
  thread = false
  type = 7
FEATURE [Part::FeaturePython] Nut022  label="M4-Nut035"  # Fasteners workbench fastener (typed FeaturePython)
  Placement = pos=(137.5,27,9) rot=(0.995904,0.090421,0;3.14159rad)
  baseObject = -> b_Base_motor_bracket_001_ [Edge85]
  diameter = 6
  invert = false
  matchOuter = false
  offset = 0
  thread = false
  type = 7
FEATURE [Part::FeaturePython] Nut023  label="M4-Nut036"  # Fasteners workbench fastener (typed FeaturePython)
  Placement = pos=(106.5,27,9) rot=(0.995904,0.090421,0;3.14159rad)
  baseObject = -> b_Base_motor_bracket_001_ [Edge89]
  diameter = 6
  invert = false
  matchOuter = false
  offset = 0
  thread = false
  type = 7
FEATURE [Part::FeaturePython] Nut024  label="M4-Nut037"  # Fasteners workbench fastener (typed FeaturePython)
  Placement = pos=(106.5,-27,9) rot=(0.995904,0.090421,0;3.14159rad)
  baseObject = -> b_Base_motor_bracket_001_ [Edge87]
  diameter = 6
  invert = false
  matchOuter = false
  offset = 0
  thread = false
  type = 7
FEATURE [Part::FeaturePython] Nut025  label="M4-Nut043"  # Fasteners workbench fastener (typed FeaturePython)
  Placement = pos=(92.8564,-8,13) rot=(-0.071945,0.997409,0;3.14159rad)
  baseObject = -> b_Base_dual_bearing_608_holder_001_ [Edge112]
  diameter = 6
  invert = false
  matchOuter = false
  offset = 0
  thread = false
  type = 7
FEATURE [Part::FeaturePython] Nut026  label="M4-Nut041"  # Fasteners workbench fastener (typed FeaturePython)
  Placement = pos=(65.1436,-8,13) rot=(-0.071945,0.997409,0;3.14159rad)
  baseObject = -> b_Base_dual_bearing_608_holder_001_ [Edge120]
  diameter = 6
  invert = false
  matchOuter = false
  offset = 0
  thread = false
  type = 7
FEATURE [Part::FeaturePython] Nut027  label="M4-Nut042"  # Fasteners workbench fastener (typed FeaturePython)
  Placement = pos=(79,16,13) rot=(-0.071945,0.997409,0;3.14159rad)
  baseObject = -> b_Base_dual_bearing_608_holder_001_ [Edge116]
  diameter = 6
  invert = false
  matchOuter = false
  offset = 0
  thread = false
  type = 7
FEATURE [Part::FeaturePython] Nut028  label="M4-Nut030"  # Fasteners workbench fastener (typed FeaturePython)
  Placement = pos=(7.49884,-10.0009,-1.9) rot=(0.291208,-0.95666,0;3.14159rad)
  baseObject = -> b_Pulley_GT2_110t1_001_ [Edge2994]
  diameter = 2
  invert = false
  matchOuter = false
  offset = 0
  thread = false
  type = 5
FEATURE [Part::FeaturePython] Nut029  label="M4-Nut031"  # Fasteners workbench fastener (typed FeaturePython)
  Placement = pos=(10.0009,7.49884,-1.9) rot=(0.291208,-0.95666,0;3.14159rad)
  baseObject = -> b_Pulley_GT2_110t1_001_ [Edge2995]
  diameter = 2
  invert = false
  matchOuter = false
  offset = 0
  thread = false
  type = 5
FEATURE [Part::FeaturePython] Nut030  label="M4-Nut032"  # Fasteners workbench fastener (typed FeaturePython)
  Placement = pos=(-10.0009,-7.49884,-1.9) rot=(0.291208,-0.95666,0;3.14159rad)
  baseObject = -> b_Pulley_GT2_110t1_001_ [Edge2993]
  diameter = 2
  invert = false
  matchOuter = false
  offset = 0
  thread = false
  type = 5
FEATURE [Part::FeaturePython] Nut031  label="M4-Nut033"  # Fasteners workbench fastener (typed FeaturePython)
  Placement = pos=(-7.49884,10.0009,-1.9) rot=(0.291208,-0.95666,0;3.14159rad)
  baseObject = -> b_Pulley_GT2_110t1_001_ [Edge14]
  diameter = 2
  invert = false
  matchOuter = false
  offset = 0
  thread = false
  type = 5
FEATURE [Part::FeaturePython] Screw018  label="M3x20-Screw"  # Fasteners workbench fastener (typed FeaturePython)
  Placement = pos=(56.3895,2.45975,33.5) rot=(-0.414583,0.910011,0;3.8e-05rad)
  baseObject = -> b_Switch_endstop1_001_ [Edge39]
  diameter = 4
  invert = true
  length = 8
  lengthCustom = 20
  matchOuter = false
  offset = 0
  thread = false
  type = 34
FEATURE [Part::FeaturePython] Screw019  label="M3x20-Screw001"  # Fasteners workbench fastener (typed FeaturePython)
  Placement = pos=(48.0011,-1.99948,33.5004) rot=(-0.414583,0.910011,0;3.8e-05rad)
  baseObject = -> b_Switch_endstop1_001_ [Edge41]
  diameter = 4
  invert = true
  length = 8
  lengthCustom = 20
  matchOuter = false
  offset = 0
  thread = false
  type = 34
FEATURE [Part::FeaturePython] Nut032  label="M3-Nut"  # Fasteners workbench fastener (typed FeaturePython)
  Placement = pos=(56.39,2.46,17.5) rot=(-1,0,0;3.14159rad)
  baseObject = -> b_Base_plate_001_ [Edge66]
  diameter = 1
  invert = false
  matchOuter = false
  offset = 0
  thread = false
  type = 5
FEATURE [Part::FeaturePython] Nut033  label="M3-Nut001"  # Fasteners workbench fastener (typed FeaturePython)
  Placement = pos=(48,-2,17.5) rot=(-1,0,0;3.14159rad)
  baseObject = -> b_Base_plate_001_ [Edge88]
  diameter = 1
  invert = false
  matchOuter = false
  offset = 0
  thread = false
  type = 5
FEATURE [Part::FeaturePython] Screw060  label="M3x8-Screw"  # Fasteners workbench fastener (typed FeaturePython)
  Placement = pos=(139.5,-15.5,5) rot=(0.995904,0.090421,0;3.14159rad)
  baseObject = -> b_Base_motor_bracket_001_ [Edge112]
  diameter = 4
  invert = true
  length = 3
  lengthCustom = 8
  matchOuter = false
  offset = 0
  thread = false
  type = 34
FEATURE [Part::FeaturePython] Screw061  label="M3x8-Screw001"  # Fasteners workbench fastener (typed FeaturePython)
  Placement = pos=(108.5,-15.5,5) rot=(0.995904,0.090421,0;3.14159rad)
  baseObject = -> b_Base_motor_bracket_001_ [Edge136]
  diameter = 4
  invert = true
  length = 3
  lengthCustom = 8
  matchOuter = false
  offset = 0
  thread = false
  type = 34
FEATURE [Part::FeaturePython] Screw062  label="M3x8-Screw002"  # Fasteners workbench fastener (typed FeaturePython)
  Placement = pos=(139.5,15.5,5) rot=(0.995904,0.090421,0;3.14159rad)
  baseObject = -> b_Base_motor_bracket_001_ [Edge122]
  diameter = 4
  invert = true
  length = 3
  lengthCustom = 8
  matchOuter = false
  offset = 0
  thread = false
  type = 34
FEATURE [Part::FeaturePython] Screw063  label="M3x8-Screw003"  # Fasteners workbench fastener (typed FeaturePython)
  Placement = pos=(108.5,15.5,5) rot=(0.995904,0.090421,0;3.14159rad)
  baseObject = -> b_Base_motor_bracket_001_ [Edge146]
  diameter = 4
  invert = true
  length = 3
  lengthCustom = 8
  matchOuter = false
  offset = 0
  thread = false
  type = 34
FEATURE [Spreadsheet::Sheet] Fasteners_BOM
  cells = A1=Type; B1=Qty; A2=DIN985 Nut M3; B2=2; A3=DIN985 Nut M4; B3=4; A4=DIN985 Nut M8; B4=1; A5=ISO4017 Screw M8x50; B5=1; A6=ISO4032 Nut M4; B6=27; A7=ISO7045 Screw M3x20; B7=2; A8=ISO7045 Screw M3x8; B8=4; A9=ISO7045 Screw M4x20; B9=13; A10=ISO7045 Screw M4x25; B10=4; A11=ISO7089 Washer M8; B11=1
FEATURE [Spreadsheet::Sheet] _PARTSLIST_  label="#PARTSLIST#"
  cells = A1=POS; B1=QTY; C1=IDENTNO; D1=DESCRIPTION; E1=SUPPLIER; F1=SUPP.IDENTNO; G1=SUPP.DESCRIPTION; H1=(FILENAME); A2=1; B2=2; C2=*; D2=*; E2=*; F2=*; G2=*; H2=Base_half-wall.FCStd; A3=2; B3=1; C3=*; D3=*; E3=*; F3=*; G3=*; H3=Base_plate.FCStd; A4=3; B4=1; C4=*; D4=*; E4=*; F4=*; G4=*; H4=Stepper NEMA 17 -  20mm shaft.step; A5=4; B5=1; C5=*; D5=*; E5=*; F5=*; G5=*; H5=Base_motor_bracket.FCStd; A6=5; B6=1; C6=*; D6=*; E6=*; F6=*; G6=*; H6=Base_dual_bearing_608_holder.FCStd; A7=6; B7=2; C7=*; D7=*; E7=*; F7=*; G7=*; H7=Ball_bearing_608.step; A8=7; B8=1; C8=*; D8=*; E8=*; F8=*; G8=*; H8=Pulley_GT2-22t_80t.step; A9=8; B9=1; C9=*; D9=*; E9=*; F9=*; G9=*; H9=Pulley_GT2-20t.step; A10=9; B10=1; C10=*; D10=*; E10=*; F10=*; G10=*; H10=Ball_bearing_6807.step; A11=10; B11=1; C11=*; D11=*; E11=*; F11=*; G11=*; H11=Thrust_bearing_51108.step; A12=11; B12=1; C12=*; D12=*; E12=*; F12=*; G12=*; H12=Pulley_GT2-110t.step; A13=12; B13=1; C13=*; D13=*; E13=*; F13=*; G13=*; H13=Belt_GT2_200mm_20-80.step; A14=13; B14=1; C14=*; D14=*; E14=*; F14=*; G14=*; H14=Belt_GT2_200mm_22-110.step; A15=14; B15=1; C15=*; D15=*; E15=*; F15=*; G15=*; H15=Switch_endstop.step
